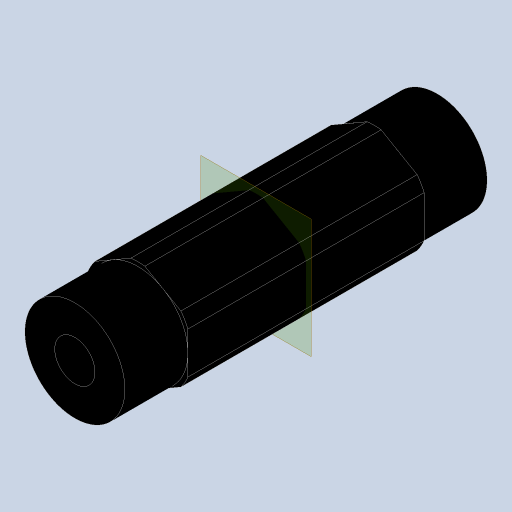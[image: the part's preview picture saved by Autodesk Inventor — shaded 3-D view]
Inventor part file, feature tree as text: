
AUTODESK INVENTOR PART (.ipt)
format: ipt  version: 2023.4 (Build 274418000, 418)  size: 172,032 bytes
history: native  units: in
note: dims shown in document units (in); Inventor stores cm internally (conversion verified against a paired STEP export)
features: extrude x3, projected_geometry x3, hole x1, mirror x1, sketch x1, plane x1
ambient origin geometry x8: Origin, YZ Plane, XZ Plane, XY Plane, X Axis, Y Axis, Z Axis, Center Point
bodies: Solid1 (feature_tree)
feature tree (10):
  extrude  "Extrusion1"  Depth=0.315in
  hole  "Hole1"  [1 undecoded]
  extrude  "Extrusion3"  Depth=0.5in
  extrude  "Extrusion4"  Depth=0.315in TaperAngle=0.0deg
  mirror  "Mirror2"
  sketch  "Sketch5"  dims[d2=0.0in d9=0.625in d10=0.385in d11=0.25in d12=0.5635in d13=1.0in d14=0.8108in d16=0.7in d17=0.0in d18=0.0in d19=0.5in d20=0.315in d21=0.0in]
  projected_geometry  "Projected Loop2"
  plane  "Work Plane1"
  projected_geometry  "Project Cut Edges1"
  projected_geometry  "Project Cut Edges2"
note: 1 required parameter value undecoded (feature->parameter linkage not recoverable at this tier; creation-order binding heuristic only, values carry confidence <= 0.55)
